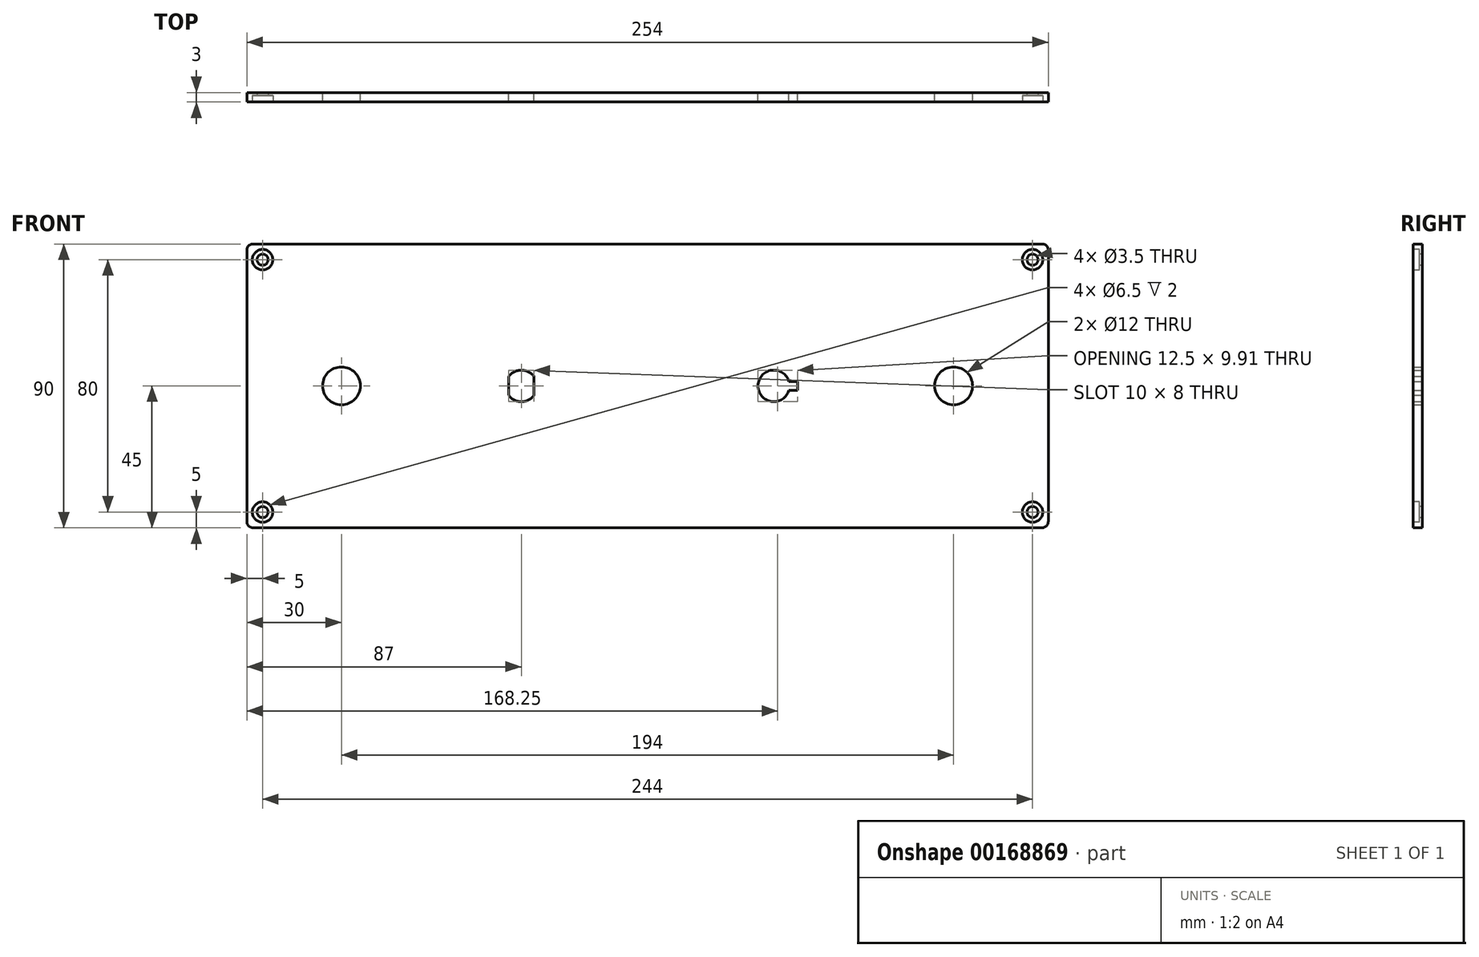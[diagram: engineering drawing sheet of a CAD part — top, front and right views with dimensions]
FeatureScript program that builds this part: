
annotation { "Feature Type Name" : "Feature", "Feature Type Description" : "" }
export const myFeature = defineFeature(function(context is Context, id is Id, definition is map)
    precondition{}
    {
        {
            var Q0;
            Q0=qCreatedBy(makeId("Front.planeOp"),FACE);
            var sketch = newSketch(context, id + "F0", { "sketchPlane" : qUnion([Q0])});
            skLineSegment(sketch, "E0.bottom", {"start": v(127, -45) * mm, "end": v(-127, -45) * mm});
            skLineSegment(sketch, "E0.top", {"start": v(127, 45) * mm, "end": v(-127, 45) * mm});
            skLineSegment(sketch, "E0.left", {"start": v(127, -45) * mm, "end": v(127, 45) * mm});
            skLineSegment(sketch, "E0.right", {"start": v(-127, -45) * mm, "end": v(-127, 45) * mm});
            skPoint(sketch, "E0.middle", {"position": v(0, 0) * mm});
            skLineSegment(sketch, "E1", {"start": v(-97, 45) * mm, "end": v(-97, -45) * mm, "construction": true});
            skLineSegment(sketch, "E2", {"start": v(-40, 45) * mm, "end": v(-40, -45) * mm, "construction": true});
            skLineSegment(sketch, "E3", {"start": v(40, 45) * mm, "end": v(40, -45) * mm, "construction": true});
            skLineSegment(sketch, "E4", {"start": v(97, 45) * mm, "end": v(97, -45) * mm, "construction": true});
            skLineSegment(sketch, "E5", {"start": v(-127, 0) * mm, "end": v(127, 0) * mm, "construction": true});
            skCircle(sketch, "E6", {"center": v(-97, 0) * mm, "radius": 6 * mm});
            skCircle(sketch, "E7", {"center": v(97, 0) * mm, "radius": 6 * mm});
            skCircle(sketch, "E8", {"center": v(40, 0) * mm, "radius": 5 * mm});
            skPoint(sketch, "E9.middle", {"position": v(45, 0) * mm});
            skLineSegment(sketch, "E10", {"start": v(-44, 3) * mm, "end": v(-44, -3) * mm});
            skLineSegment(sketch, "E11", {"start": v(-36, 3) * mm, "end": v(-36, -3) * mm});
            skLineSegment(sketch, "E12.bottom", {"start": v(47.5, -1.35) * mm, "end": v(42.5, -1.35) * mm});
            skLineSegment(sketch, "E12.top", {"start": v(47.5, 1.35) * mm, "end": v(42.5, 1.35) * mm});
            skLineSegment(sketch, "E12.left", {"start": v(47.5, -1.35) * mm, "end": v(47.5, 1.35) * mm});
            skLineSegment(sketch, "E12.right", {"start": v(42.5, -1.35) * mm, "end": v(42.5, 1.35) * mm});
            skArc(sketch, "E13", {"start": v(-44, 3) * mm, "mid": v(-40, 5) * mm, "end": v(-36, 3) * mm});
            skArc(sketch, "E14", {"start": v(-36, -3) * mm, "mid": v(-40, -5) * mm, "end": v(-44, -3) * mm});
            skCircle(sketch, "E15", {"center": v(-40, 0) * mm, "radius": 25 * mm, "construction": true});
            skCircle(sketch, "E16", {"center": v(40, 0) * mm, "radius": 25 * mm, "construction": true});
            skLineSegment(sketch, "E17", {"start": v(-67.5, 47.14) * mm, "end": v(-67.5, -53.68) * mm, "construction": true});
            skLineSegment(sketch, "E18.MirrorCS", {"start": v(-12.5, 47.14) * mm, "end": v(-12.5, -53.68) * mm, "construction": true});
            skSolve(sketch);
        }
        {
            var Q0;
            Q0=makeQuery(id+"F0.imprint","IMPRINT",FACE,{"disambiguationData":[TD([[makeQuery(id+"F0.imprint","IMPRINT",EDGE,{"derivedFrom":sQuery(id+"F0.wireOp",EDGE,"E0.bottom")}),-1.0]])]});
            extrude(context, id + "F1", {"entities" : qUnion([Q0]), "depth" : 3 * mm});
        }
        {
            var Q0;
            Q0=makeQuery(id+"F1.opExtrude","CAP_FACE",FACE,{"disambiguationData":[OSD([sQuery(id+"F0.wireOp",EDGE,"E0.bottom"),sQuery(id+"F0.wireOp",EDGE,"E0.top"),sQuery(id+"F0.wireOp",EDGE,"E0.left"),sQuery(id+"F0.wireOp",EDGE,"E0.right"),sQuery(id+"F0.wireOp",EDGE,"E6"),sQuery(id+"F0.wireOp",EDGE,"E7"),sQuery(id+"F0.wireOp",EDGE,"E8"),sQuery(id+"F0.wireOp",EDGE,"E10"),sQuery(id+"F0.wireOp",EDGE,"E11"),sQuery(id+"F0.wireOp",EDGE,"E12.bottom"),sQuery(id+"F0.wireOp",EDGE,"E12.top"),sQuery(id+"F0.wireOp",EDGE,"E12.left"),sQuery(id+"F0.wireOp",EDGE,"E13"),sQuery(id+"F0.wireOp",EDGE,"E14")])],"isStart":false});
            var sketch = newSketch(context, id + "F2", { "sketchPlane" : qUnion([Q0])});
            skLineSegment(sketch, "E19", {"start": v(-131.72, 40) * mm, "end": v(130.27, 40) * mm, "construction": true});
            skLineSegment(sketch, "E20", {"start": v(-122, 50.14) * mm, "end": v(-122, -51.56) * mm, "construction": true});
            skLineSegment(sketch, "E21.MirrorCS", {"start": v(-131.72, -40) * mm, "end": v(130.27, -40) * mm, "construction": true});
            skLineSegment(sketch, "E22.MirrorCS", {"start": v(122, 50.14) * mm, "end": v(122, -51.56) * mm, "construction": true});
            skPoint(sketch, "E23", {"position": v(-122, 40) * mm});
            skPoint(sketch, "E24", {"position": v(122, 40) * mm});
            skPoint(sketch, "E25", {"position": v(122, -40) * mm});
            skPoint(sketch, "E26", {"position": v(-122, -40) * mm});
            skSolve(sketch);
        }
        {
            var Q0;
            Q0=sQuery(id+"F2.wireOp",VERTEX,"E23");
            var Q1;
            Q1=sQuery(id+"F2.wireOp",VERTEX,"E26");
            var Q2;
            Q2=sQuery(id+"F2.wireOp",VERTEX,"E24");
            var Q3;
            Q3=sQuery(id+"F2.wireOp",VERTEX,"E25");
            var Q4;
            Q4=makeQuery(id+"F1.opExtrude","SWEPT_BODY",BODY,{"disambiguationData":[OSD([sQuery(id+"F0.wireOp",EDGE,"E0.bottom"),sQuery(id+"F0.wireOp",EDGE,"E0.top"),sQuery(id+"F0.wireOp",EDGE,"E0.left"),sQuery(id+"F0.wireOp",EDGE,"E0.right"),sQuery(id+"F0.wireOp",EDGE,"E6"),sQuery(id+"F0.wireOp",EDGE,"E7"),sQuery(id+"F0.wireOp",EDGE,"E8"),sQuery(id+"F0.wireOp",EDGE,"E10"),sQuery(id+"F0.wireOp",EDGE,"E11"),sQuery(id+"F0.wireOp",EDGE,"E12.bottom"),sQuery(id+"F0.wireOp",EDGE,"E12.top"),sQuery(id+"F0.wireOp",EDGE,"E12.left"),sQuery(id+"F0.wireOp",EDGE,"E13"),sQuery(id+"F0.wireOp",EDGE,"E14")])]});
            hole(context, id + "F3", {"style" : HoleStyle.C_BORE, "endStyle" : HoleEndStyle.THROUGH, "holeDiameter" : 3.5 * mm, "cBoreDiameter" : 6.5 * mm, "cBoreDepth" : 2 * mm, "locations" : qUnion([Q0, Q1, Q2, Q3]), "scope" : qUnion([Q4]), "isTappedThrough" : true});
        }
        {
            var Q0;
            Q0=makeQuery(id+"F1.opExtrude","SWEPT_EDGE",EDGE,{"disambiguationData":[OSD([sQuery(id+"F0.wireOp",EDGE,"E0.top"),sQuery(id+"F0.wireOp",EDGE,"E0.right")])]});
            var Q1;
            Q1=makeQuery(id+"F1.opExtrude","SWEPT_EDGE",EDGE,{"disambiguationData":[OSD([sQuery(id+"F0.wireOp",EDGE,"E0.bottom"),sQuery(id+"F0.wireOp",EDGE,"E0.right")])]});
            var Q2;
            Q2=makeQuery(id+"F1.opExtrude","SWEPT_EDGE",EDGE,{"disambiguationData":[OSD([sQuery(id+"F0.wireOp",EDGE,"E0.bottom"),sQuery(id+"F0.wireOp",EDGE,"E0.left")])]});
            var Q3;
            Q3=makeQuery(id+"F1.opExtrude","SWEPT_EDGE",EDGE,{"disambiguationData":[OSD([sQuery(id+"F0.wireOp",EDGE,"E0.top"),sQuery(id+"F0.wireOp",EDGE,"E0.left")])]});
            fillet(context, id + "F4", {"entities" : qUnion([Q0, Q1, Q2, Q3]), "radius" : 2 * mm, "tangentPropagation" : true, "allowEdgeOverflow" : false});
        }
    });
